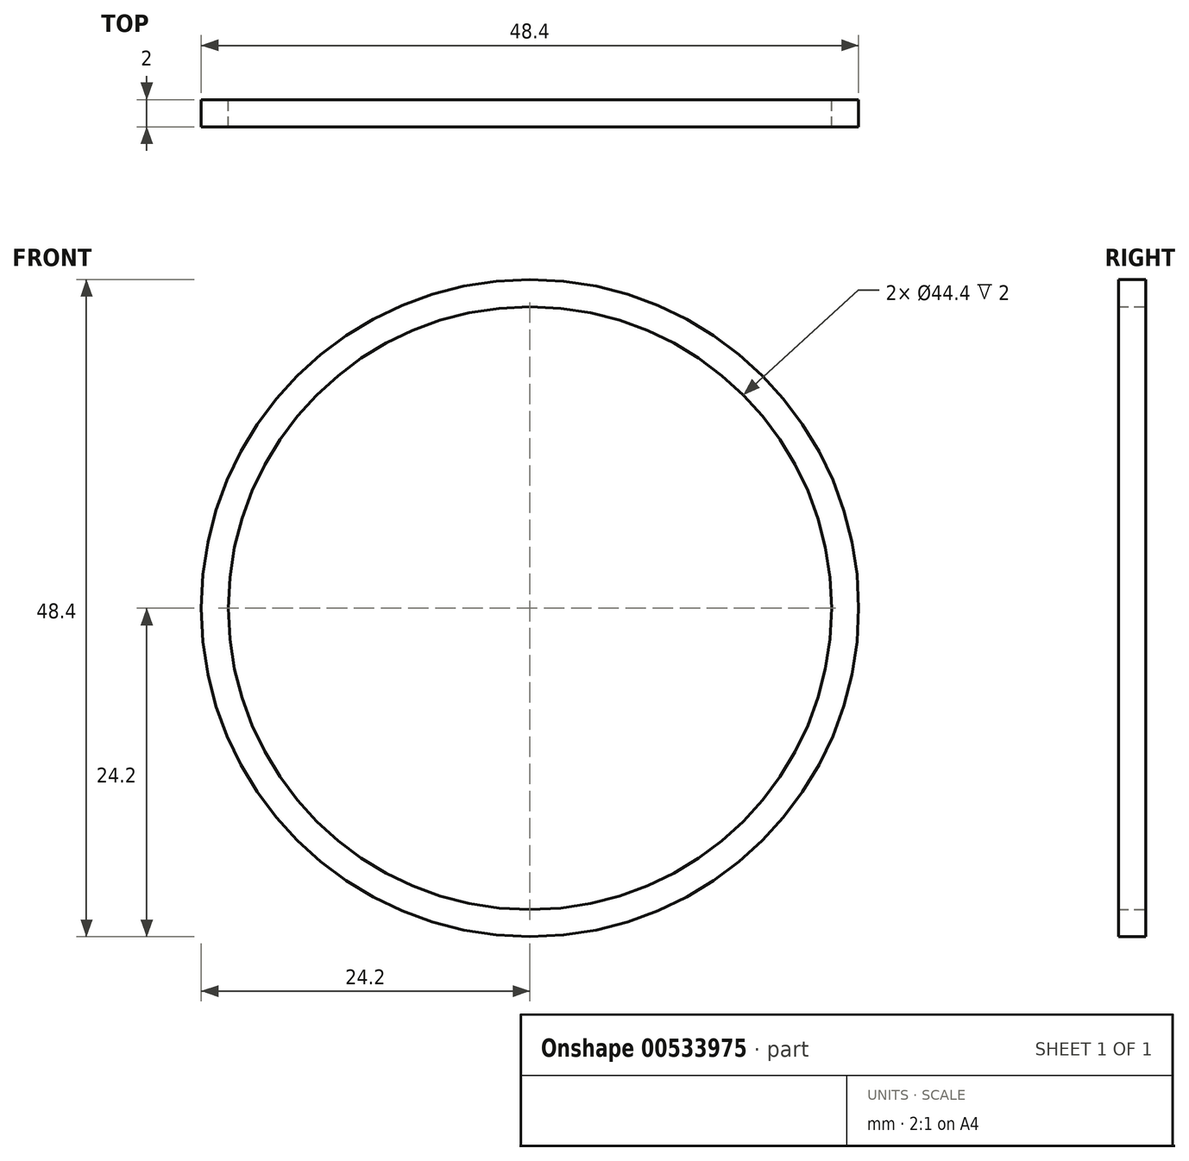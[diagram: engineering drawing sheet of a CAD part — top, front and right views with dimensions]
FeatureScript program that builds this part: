
annotation { "Feature Type Name" : "Feature", "Feature Type Description" : "" }
export const myFeature = defineFeature(function(context is Context, id is Id, definition is map)
    precondition{}
    {
        {
            var Q0;
            Q0=qCreatedBy(makeId("Front.planeOp"),FACE);
            var sketch = newSketch(context, id + "F0", { "sketchPlane" : qUnion([Q0])});
            skCircle(sketch, "E0", {"center": v(0, 0) * mm, "radius": 22.2 * mm});
            skCircle(sketch, "E1", {"center": v(0, 0) * mm, "radius": 24.2 * mm});
            skSolve(sketch);
        }
        {
            var Q0;
            Q0=makeQuery(id+"F0.imprint","IMPRINT",FACE,{"disambiguationData":[TD([[makeQuery(id+"F0.imprint","IMPRINT",EDGE,{"derivedFrom":sQuery(id+"F0.wireOp",EDGE,"E0")}),-1.0]])]});
            extrude(context, id + "F1", {"entities" : qUnion([Q0]), "depth" : 2 * mm, "offsetDistance" : 25 * mm});
        }
    });
